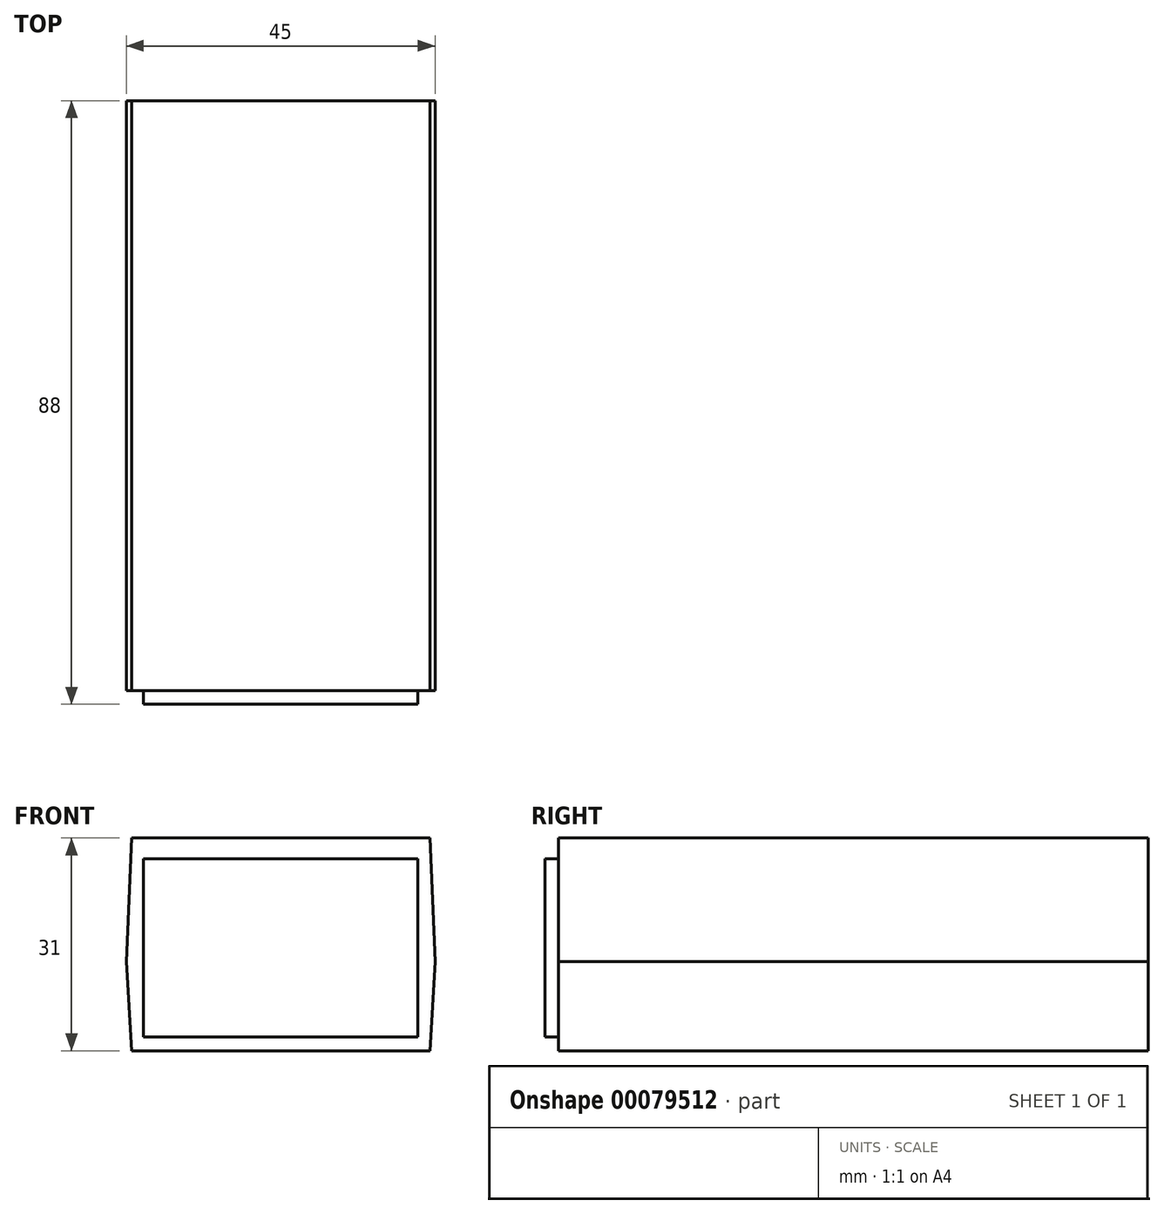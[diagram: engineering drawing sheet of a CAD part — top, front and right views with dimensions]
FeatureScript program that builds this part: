
annotation { "Feature Type Name" : "Feature", "Feature Type Description" : "" }
export const myFeature = defineFeature(function(context is Context, id is Id, definition is map)
    precondition{}
    {
        {
            var Q0;
            Q0=qCreatedBy(makeId("Front.planeOp"),FACE);
            var sketch = newSketch(context, id + "F0", { "sketchPlane" : qUnion([Q0])});
            skLineSegment(sketch, "E0", {"start": v(-21.75, 0) * mm, "end": v(-22.5, 13) * mm});
            skLineSegment(sketch, "E1", {"start": v(-22.5, 13) * mm, "end": v(-21.75, 31) * mm});
            skLineSegment(sketch, "E2", {"start": v(-21.75, 31) * mm, "end": v(21.75, 31) * mm});
            skLineSegment(sketch, "E3", {"start": v(21.75, 31) * mm, "end": v(22.5, 13) * mm});
            skLineSegment(sketch, "E4", {"start": v(22.5, 13) * mm, "end": v(21.75, 0) * mm});
            skLineSegment(sketch, "E5", {"start": v(21.75, 0) * mm, "end": v(-21.75, 0) * mm});
            skSolve(sketch);
        }
        {
            var Q0;
            Q0 = qSketchRegion(id + "F0", true);
            extrude(context, id + "F1", {"entities" : qUnion([Q0]), "depth" : 86 * mm});
        }
        {
            var Q0;
            Q0=makeQuery(id+"F1.opExtrude","CAP_FACE",FACE,{"disambiguationData":[OSD([sQuery(id+"F0.wireOp",EDGE,"E0"),sQuery(id+"F0.wireOp",EDGE,"E1"),sQuery(id+"F0.wireOp",EDGE,"E2"),sQuery(id+"F0.wireOp",EDGE,"E3"),sQuery(id+"F0.wireOp",EDGE,"E4"),sQuery(id+"F0.wireOp",EDGE,"E5")])],"isStart":false});
            var sketch = newSketch(context, id + "F2", { "sketchPlane" : qUnion([Q0])});
            skLineSegment(sketch, "E6.bottom", {"start": v(-20, 28) * mm, "end": v(20, 28) * mm});
            skLineSegment(sketch, "E6.top", {"start": v(-20, 2) * mm, "end": v(20, 2) * mm});
            skLineSegment(sketch, "E6.left", {"start": v(-20, 28) * mm, "end": v(-20, 2) * mm});
            skLineSegment(sketch, "E6.right", {"start": v(20, 28) * mm, "end": v(20, 2) * mm});
            skSolve(sketch);
        }
        {
            var Q0;
            Q0=makeQuery(id+"F2.imprint","IMPRINT",FACE,{"disambiguationData":[TD([[makeQuery(id+"F2.imprint","IMPRINT",EDGE,{"derivedFrom":sQuery(id+"F2.wireOp",EDGE,"E6.bottom")}),-1.0]])]});
            extrude(context, id + "F3", {"entities" : qUnion([Q0]), "operationType" : NewBodyOperationType.ADD, "depth" : 2 * mm});
        }
    });
